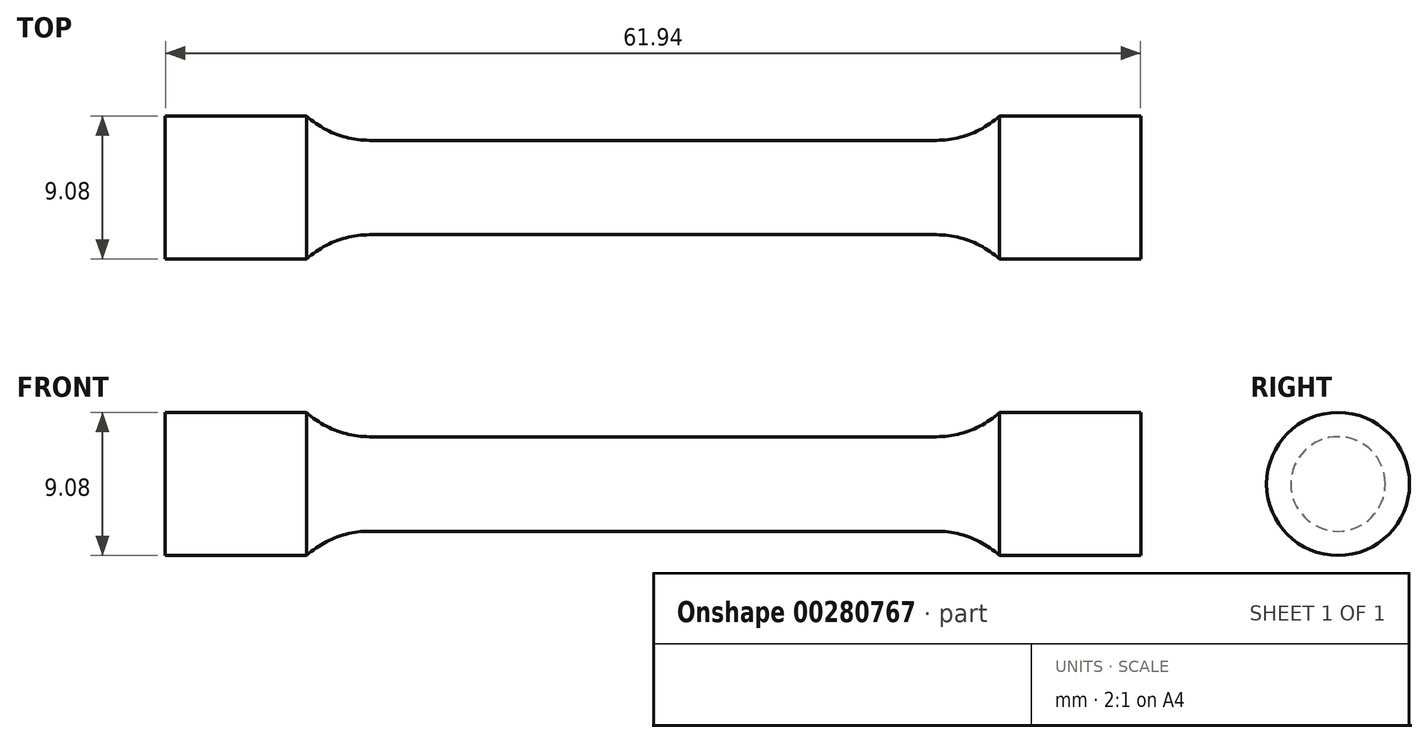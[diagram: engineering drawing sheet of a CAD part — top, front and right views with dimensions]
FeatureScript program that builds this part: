
annotation { "Feature Type Name" : "Feature", "Feature Type Description" : "" }
export const myFeature = defineFeature(function(context is Context, id is Id, definition is map)
    precondition{}
    {
        {
            var Q0;
            Q0=qCreatedBy(makeId("Front.planeOp"),FACE);
            var sketch = newSketch(context, id + "F0", { "sketchPlane" : qUnion([Q0])});
            skLineSegment(sketch, "E0", {"start": v(0, 3) * mm, "end": v(18, 3) * mm});
            skArc(sketch, "E1", {"start": v(18, 3) * mm, "mid": v(20.15, 3.4) * mm, "end": v(22.01, 4.54) * mm});
            skLineSegment(sketch, "E2", {"start": v(22.01, 4.54) * mm, "end": v(30.97, 4.54) * mm});
            skLineSegment(sketch, "E3", {"start": v(30.97, 4.54) * mm, "end": v(30.97, 0) * mm});
            skLineSegment(sketch, "E4.MirrorCS", {"start": v(-30.97, 4.54) * mm, "end": v(-30.97, 0) * mm});
            skArc(sketch, "E5.MirrorCS", {"start": v(-18, 3) * mm, "mid": v(-20.15, 3.4) * mm, "end": v(-22.01, 4.54) * mm});
            skLineSegment(sketch, "E6.MirrorCS", {"start": v(0, 3) * mm, "end": v(-18, 3) * mm});
            skLineSegment(sketch, "E7.MirrorCS", {"start": v(-22.01, 4.54) * mm, "end": v(-30.97, 4.54) * mm});
            skLineSegment(sketch, "E8", {"start": v(-30.97, 0) * mm, "end": v(30.97, 0) * mm});
            skSolve(sketch);
        }
        {
            var Q0;
            Q0=makeQuery(id+"F0.imprint","IMPRINT",FACE,{"disambiguationData":[TD([[makeQuery(id+"F0.imprint","IMPRINT",EDGE,{"derivedFrom":sQuery(id+"F0.wireOp",EDGE,"E0")}),-1.0]])]});
            var Q1;
            Q1=sQuery(id+"F0.wireOp",EDGE,"E8");
            revolve(context, id + "F1", {"entities" : qUnion([Q0]), "axis" : qUnion([Q1]), "revolveType" : RevolveType.FULL});
        }
    });
